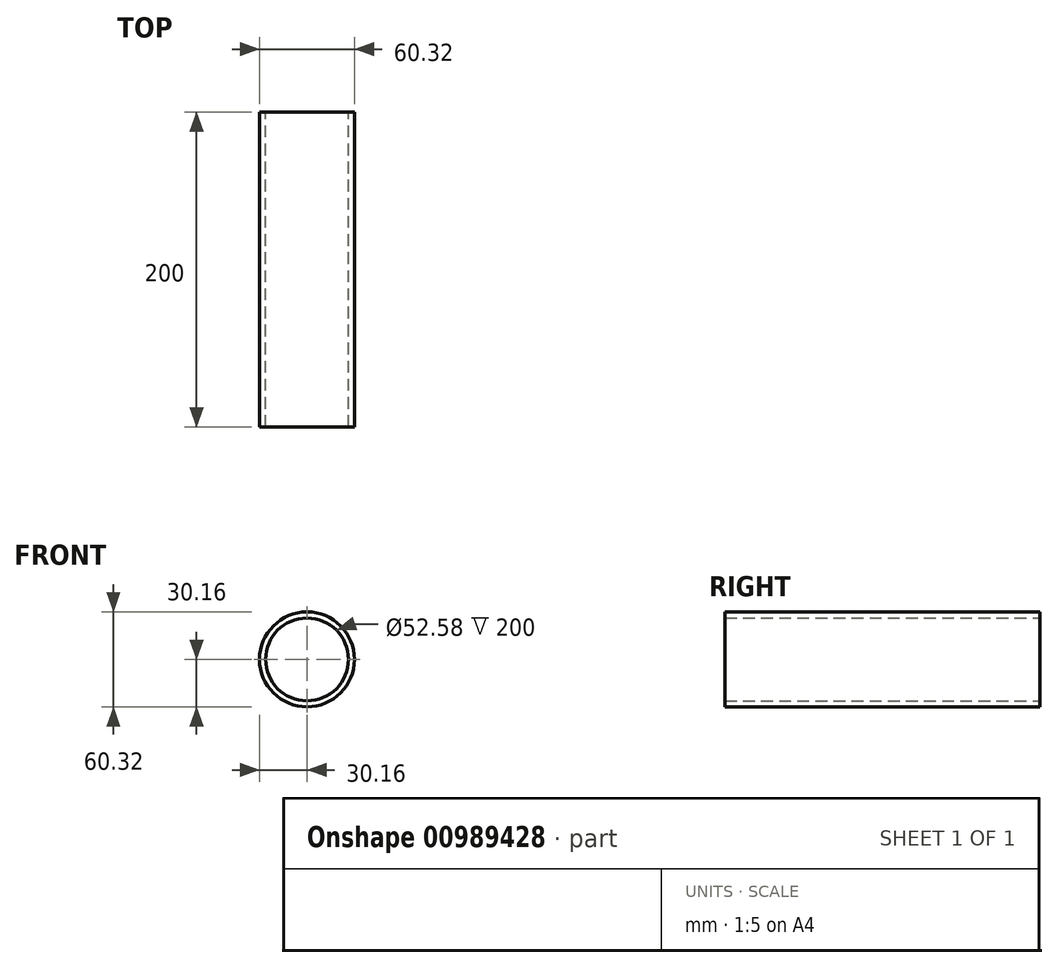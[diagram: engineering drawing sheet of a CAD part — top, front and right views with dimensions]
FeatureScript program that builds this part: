
annotation { "Feature Type Name" : "Feature", "Feature Type Description" : "" }
export const myFeature = defineFeature(function(context is Context, id is Id, definition is map)
    precondition{}
    {
        {
            var Q0;
            Q0=qCreatedBy(makeId("Front.planeOp"),FACE);
            var sketch = newSketch(context, id + "F0", { "sketchPlane" : qUnion([Q0])});
            skCircle(sketch, "E0", {"center": v(0, 0) * mm, "radius": 30.16 * mm});
            skCircle(sketch, "E1", {"center": v(0, 0) * mm, "radius": 26.29 * mm});
            skSolve(sketch);
        }
        {
            var Q0;
            Q0 = qSketchRegion(id + "F0", true);
            extrude(context, id + "F1", {"entities" : qUnion([Q0]), "depth" : 200 * mm, "offsetDistance" : 25 * mm});
        }
    });
